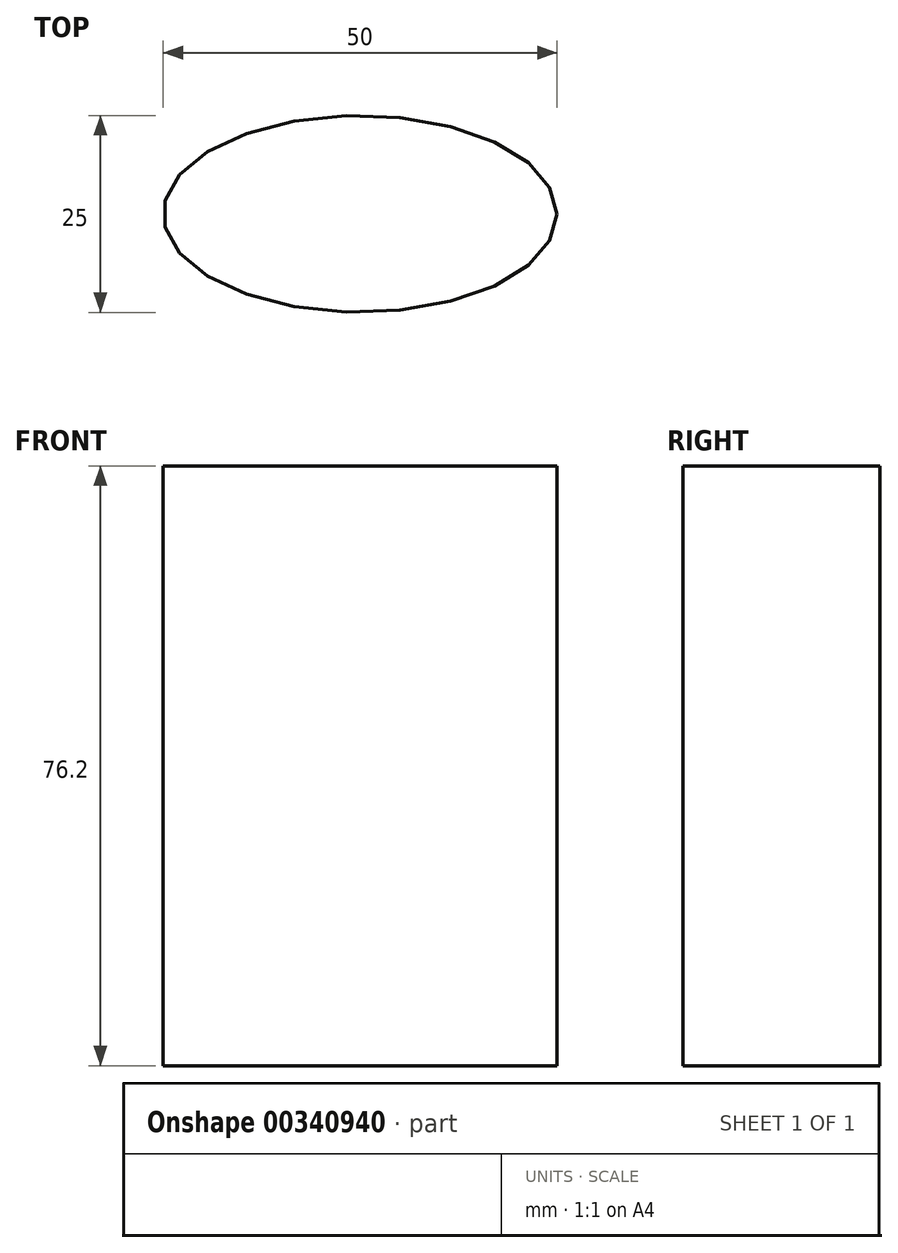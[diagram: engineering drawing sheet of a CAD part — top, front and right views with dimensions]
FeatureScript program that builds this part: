
annotation { "Feature Type Name" : "Feature", "Feature Type Description" : "" }
export const myFeature = defineFeature(function(context is Context, id is Id, definition is map)
    precondition{}
    {
        {
            var Q0;
            Q0=qCreatedBy(makeId("Top.planeOp"),FACE);
            var sketch = newSketch(context, id + "F0", { "sketchPlane" : qUnion([Q0])});
            skEllipse(sketch, "E0", {"center": v(0, 0) * mm, "majorRadius": 25 * mm, "minorRadius": 12.5 * mm, "majorAxis": v(1, 0)});
            skSolve(sketch);
        }
        {
            var Q0;
            Q0 = qSketchRegion(id + "F0", true);
            extrude(context, id + "F1", {"entities" : qUnion([Q0]), "depth" : 76.2 * mm});
        }
    });
